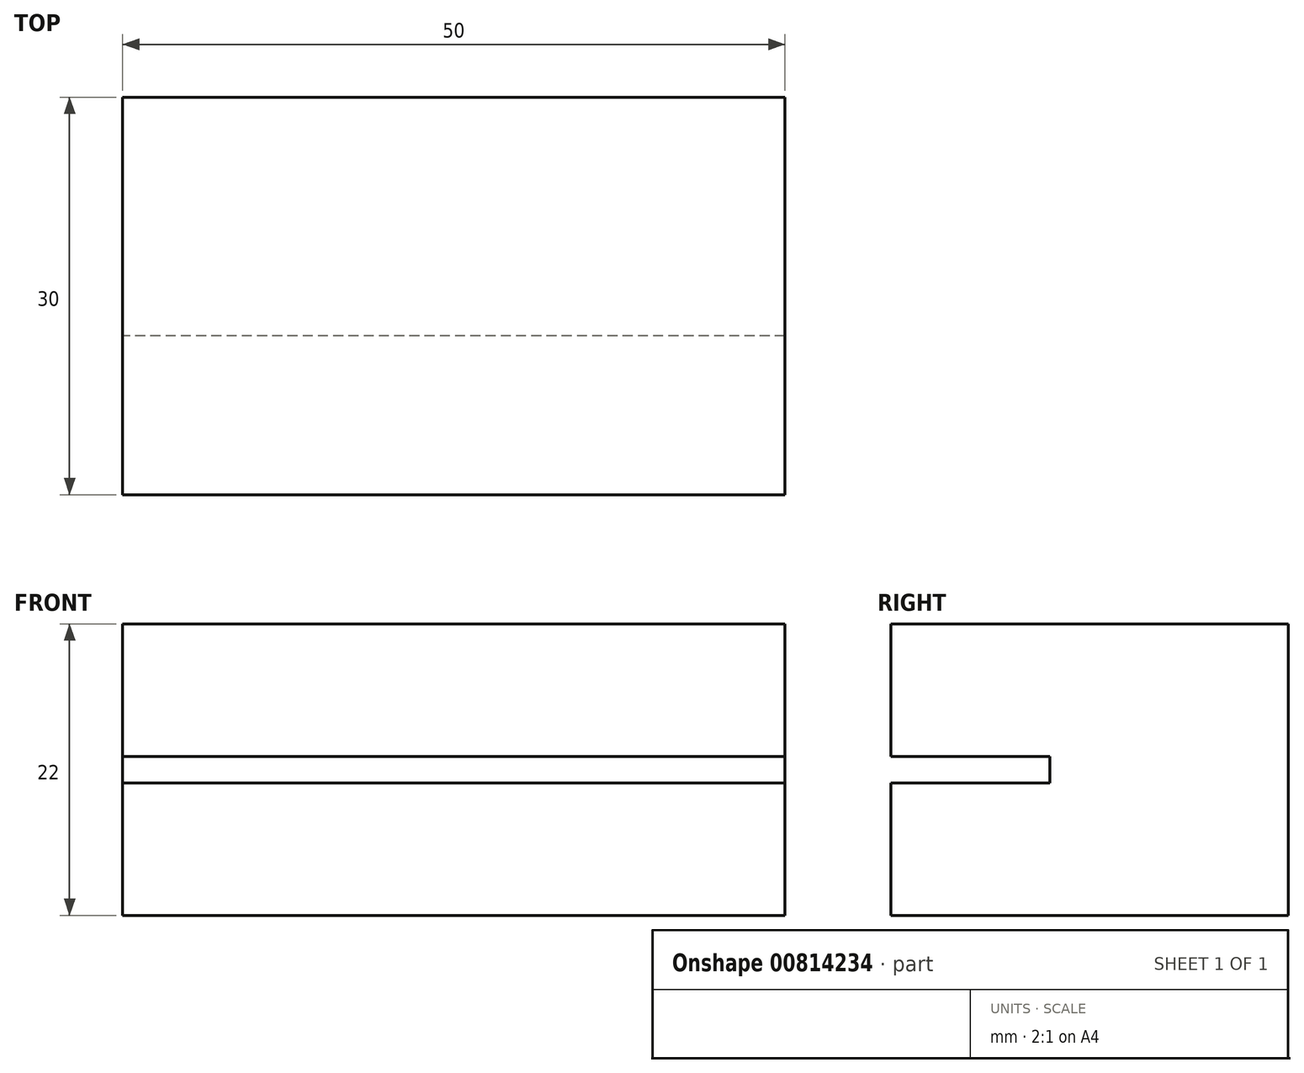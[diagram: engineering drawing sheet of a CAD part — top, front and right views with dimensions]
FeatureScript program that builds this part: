
annotation { "Feature Type Name" : "Feature", "Feature Type Description" : "" }
export const myFeature = defineFeature(function(context is Context, id is Id, definition is map)
    precondition{}
    {
        {
            var Q0;
            Q0=qCreatedBy(makeId("Top.planeOp"),FACE);
            var sketch = newSketch(context, id + "F0", { "sketchPlane" : qUnion([Q0])});
            skLineSegment(sketch, "E0.bottom", {"start": v(0, 0) * mm, "end": v(-50, 0) * mm});
            skLineSegment(sketch, "E0.top", {"start": v(0, 30) * mm, "end": v(-50, 30) * mm});
            skLineSegment(sketch, "E0.left", {"start": v(0, 0) * mm, "end": v(0, 30) * mm});
            skLineSegment(sketch, "E0.right", {"start": v(-50, 0) * mm, "end": v(-50, 30) * mm});
            skLineSegment(sketch, "E1.bottom", {"start": v(0, 0) * mm, "end": v(30, 0) * mm});
            skLineSegment(sketch, "E1.top", {"start": v(0, -30) * mm, "end": v(30, -30) * mm});
            skLineSegment(sketch, "E1.left", {"start": v(0, 0) * mm, "end": v(0, -30) * mm});
            skLineSegment(sketch, "E1.right", {"start": v(30, 0) * mm, "end": v(30, -30) * mm});
            skLineSegment(sketch, "E2", {"start": v(0, 30) * mm, "end": v(30, 0) * mm});
            skCircle(sketch, "E3", {"center": v(15.14, 17.69) * mm, "radius": 2 * mm});
            skCircle(sketch, "E4", {"center": v(15.14, 17.69) * mm, "radius": 4 * mm});
            skSolve(sketch);
        }
        {
            var Q0;
            Q0=makeQuery(id+"F0.imprint","IMPRINT",FACE,{"disambiguationData":[TD([[makeQuery(id+"F0.imprint","IMPRINT",EDGE,{"derivedFrom":sQuery(id+"F0.wireOp",EDGE,"E1.bottom")}),-1.0]])]});
            var Q1;
            Q1=makeQuery(id+"F0.imprint","IMPRINT",FACE,{"disambiguationData":[TD([[makeQuery(id+"F0.imprint","IMPRINT",EDGE,{"derivedFrom":sQuery(id+"F0.wireOp",EDGE,"E0.left")}),-1.0]])]});
            var Q2;
            Q2=makeQuery(id+"F0.imprint","IMPRINT",FACE,{"disambiguationData":[TD([[makeQuery(id+"F0.imprint","IMPRINT",EDGE,{"derivedFrom":sQuery(id+"F0.wireOp",EDGE,"E0.bottom")}),-1.0]])]});
            extrude(context, id + "F1", {"entities" : qUnion([Q0, Q1, Q2]), "depth" : 12 * mm, "offsetDistance" : 25 * mm});
        }
        {
            var Q0;
            Q0=makeQuery(id+"F1.opExtrude","CAP_FACE",FACE,{"disambiguationData":[OSD([sQuery(id+"F0.wireOp",EDGE,"E0.bottom"),sQuery(id+"F0.wireOp",EDGE,"E0.top"),sQuery(id+"F0.wireOp",EDGE,"E0.right"),sQuery(id+"F0.wireOp",EDGE,"E1.top"),sQuery(id+"F0.wireOp",EDGE,"E1.left"),sQuery(id+"F0.wireOp",EDGE,"E1.right"),sQuery(id+"F0.wireOp",EDGE,"E2")])],"isStart":false});
            var sketch = newSketch(context, id + "F2", { "sketchPlane" : qUnion([Q0])});
            skLineSegment(sketch, "E5.bottom", {"start": v(-50, 0) * mm, "end": v(16.32, 0) * mm});
            skLineSegment(sketch, "E5.top", {"start": v(-50, 12) * mm, "end": v(16.32, 12) * mm});
            skLineSegment(sketch, "E5.left", {"start": v(-50, 0) * mm, "end": v(-50, 12) * mm});
            skLineSegment(sketch, "E5.right", {"start": v(16.32, 0) * mm, "end": v(16.32, 12) * mm});
            skLineSegment(sketch, "E6.bottom", {"start": v(0, -30) * mm, "end": v(12, -30) * mm});
            skLineSegment(sketch, "E6.top", {"start": v(0, 12) * mm, "end": v(12, 12) * mm});
            skLineSegment(sketch, "E6.left", {"start": v(0, -30) * mm, "end": v(0, 12) * mm});
            skLineSegment(sketch, "E6.right", {"start": v(12, -30) * mm, "end": v(12, 12) * mm});
            skSolve(sketch);
        }
        {
            var Q0;
            {var subQ5=sQuery(id+"F2.wireOp",EDGE,"E6.bottom");Q0=makeQuery(id+"F2.imprint","IMPRINT",FACE,{"disambiguationData":[TD([[makeQuery(id+"F2.imprint","IMPRINT",EDGE,{"derivedFrom":subQ5}),1.0]])]});}
            var Q1;
            {var subQ5=sQuery(id+"F2.wireOp",EDGE,"E6.top");Q1=makeQuery(id+"F2.imprint","IMPRINT",FACE,{"disambiguationData":[TD([[makeQuery(id+"F2.imprint","IMPRINT",EDGE,{"derivedFrom":subQ5}),-1.0]])]});}
            var Q2;
            {var subQ3=sQuery(id+"F2.wireOp",EDGE,"E5.left");Q2=makeQuery(id+"F2.imprint","IMPRINT",FACE,{"disambiguationData":[TD([[makeQuery(id+"F2.imprint","IMPRINT",EDGE,{"derivedFrom":subQ3}),-1.0]])]});}
            extrude(context, id + "F3", {"entities" : qUnion([Q0, Q1, Q2]), "operationType" : NewBodyOperationType.REMOVE, "oppositeDirection" : true, "depth" : 3.5 * mm, "offsetDistance" : 25 * mm});
        }
        {
            var Q0;
            Q0=makeQuery(id+"F1.opExtrude","CAP_FACE",FACE,{"disambiguationData":[OSD([sQuery(id+"F0.wireOp",EDGE,"E0.bottom"),sQuery(id+"F0.wireOp",EDGE,"E0.top"),sQuery(id+"F0.wireOp",EDGE,"E0.right"),sQuery(id+"F0.wireOp",EDGE,"E1.top"),sQuery(id+"F0.wireOp",EDGE,"E1.left"),sQuery(id+"F0.wireOp",EDGE,"E1.right"),sQuery(id+"F0.wireOp",EDGE,"E2")])],"isStart":false});
            var sketch = newSketch(context, id + "F4", { "sketchPlane" : qUnion([Q0])});
            skLineSegment(sketch, "E7.bottom", {"start": v(-50, 30) * mm, "end": v(0, 30) * mm});
            skLineSegment(sketch, "E7.top", {"start": v(-50, 0) * mm, "end": v(0, 0) * mm});
            skLineSegment(sketch, "E7.left", {"start": v(-50, 30) * mm, "end": v(-50, 0) * mm});
            skLineSegment(sketch, "E7.right", {"start": v(0, 30) * mm, "end": v(0, 0) * mm});
            skLineSegment(sketch, "E8.bottom", {"start": v(0, 0) * mm, "end": v(30, 0) * mm});
            skLineSegment(sketch, "E8.top", {"start": v(0, -30) * mm, "end": v(30, -30) * mm});
            skLineSegment(sketch, "E8.left", {"start": v(0, 0) * mm, "end": v(0, -30) * mm});
            skLineSegment(sketch, "E8.right", {"start": v(30, 0) * mm, "end": v(30, -30) * mm});
            skLineSegment(sketch, "E9", {"start": v(0, 30) * mm, "end": v(11.74, 18.26) * mm});
            skSolve(sketch);
        }
        {
            var Q0;
            {var subQ0=sQuery(id+"F4.wireOp",EDGE,"E7.top");Q0=makeQuery(id+"F4.imprint","IMPRINT",FACE,{"disambiguationData":[TD([[makeQuery(id+"F4.imprint","IMPRINT",EDGE,{"derivedFrom":subQ0}),1.0]])]});}
            var Q1;
            {var subQ0=sQuery(id+"F4.wireOp",EDGE,"E8.left");Q1=makeQuery(id+"F4.imprint","IMPRINT",FACE,{"disambiguationData":[TD([[makeQuery(id+"F4.imprint","IMPRINT",EDGE,{"derivedFrom":subQ0}),1.0]])]});}
            var Q2;
            {var subQ3=sQuery(id+"F4.wireOp",EDGE,"E9");Q2=makeQuery(id+"F4.imprint","IMPRINT",FACE,{"disambiguationData":[TD([[makeQuery(id+"F4.imprint","IMPRINT",EDGE,{"derivedFrom":subQ3}),-1.0]])]});}
            var Q3;
            {var subQ0=sQuery(id+"F4.wireOp",EDGE,"E8.bottom");var subQ5=makeQuery(id+"F3.boolean.opBoolean","COPY",EDGE,{"derivedFrom":makeQuery(id+"F3.opExtrude","CAP_EDGE",EDGE,{"disambiguationData":[OSD([sQuery(id+"F2.wireOp",EDGE,"E6.right")])],"isStart":true})});var subQ7=makeQuery(id+"F4.imprint","INTERSECT",VERTEX,{"derivedFrom":[subQ5,subQ0]});Q3=makeQuery(id+"F4.imprint","IMPRINT",FACE,{"disambiguationData":[TD([[makeQuery(id+"F4.imprint","IMPRINT",EDGE,{"disambiguationData":[TD([[subQ7,-1.0]])],"derivedFrom":subQ5}),1.0]])]});}
            var Q4;
            {var subQ0=sQuery(id+"F4.wireOp",EDGE,"E7.bottom");Q4=makeQuery(id+"F4.imprint","IMPRINT",FACE,{"disambiguationData":[TD([[makeQuery(id+"F4.imprint","IMPRINT",EDGE,{"derivedFrom":subQ0}),1.0]])]});}
            var Q5;
            {var subQ0=sQuery(id+"F4.wireOp",EDGE,"E8.right");Q5=makeQuery(id+"F4.imprint","IMPRINT",FACE,{"disambiguationData":[TD([[makeQuery(id+"F4.imprint","IMPRINT",EDGE,{"derivedFrom":subQ0}),-1.0]])]});}
            extrude(context, id + "F5", {"entities" : qUnion([Q0, Q1, Q2, Q3, Q4, Q5]), "operationType" : NewBodyOperationType.ADD, "depth" : 10 * mm, "offsetDistance" : 25 * mm});
        }
        {
            var Q0;
            Q0=qSketchRegion(id+"F0",true);
            extrude(context, id + "F6", {"entities" : qUnion([Q0]), "operationType" : NewBodyOperationType.ADD, "depth" : 10 * mm, "offsetDistance" : 25 * mm});
        }
        {
            var Q0;
            Q0=makeQuery(id+"F5.opExtrude","CAP_FACE",FACE,{"disambiguationData":[OSD([sQuery(id+"F0.wireOp",EDGE,"E2"),sQuery(id+"F0.wireOp",EDGE,"E4"),sQuery(id+"F4.wireOp",EDGE,"E7.bottom"),sQuery(id+"F4.wireOp",EDGE,"E7.top"),sQuery(id+"F4.wireOp",EDGE,"E7.left"),sQuery(id+"F4.wireOp",EDGE,"E8.top"),sQuery(id+"F4.wireOp",EDGE,"E8.left"),sQuery(id+"F4.wireOp",EDGE,"E8.right"),sQuery(id+"F4.wireOp",EDGE,"E9")])],"isStart":false});
            var sketch = newSketch(context, id + "F7", { "sketchPlane" : qUnion([Q0])});
            skLineSegment(sketch, "E10.bottom", {"start": v(0, 30) * mm, "end": v(30, 30) * mm});
            skLineSegment(sketch, "E10.top", {"start": v(0, -35.1) * mm, "end": v(30, -35.1) * mm});
            skLineSegment(sketch, "E10.left", {"start": v(0, 30) * mm, "end": v(0, -35.1) * mm});
            skLineSegment(sketch, "E10.right", {"start": v(30, 30) * mm, "end": v(30, -35.1) * mm});
            skSolve(sketch);
        }
        {
            var Q0;
            Q0 = qSketchRegion(id + "F7", true);
            extrude(context, id + "F8", {"entities" : qUnion([Q0]), "operationType" : NewBodyOperationType.REMOVE, "oppositeDirection" : true, "depth" : 25 * mm, "offsetDistance" : 25 * mm});
        }
    });
